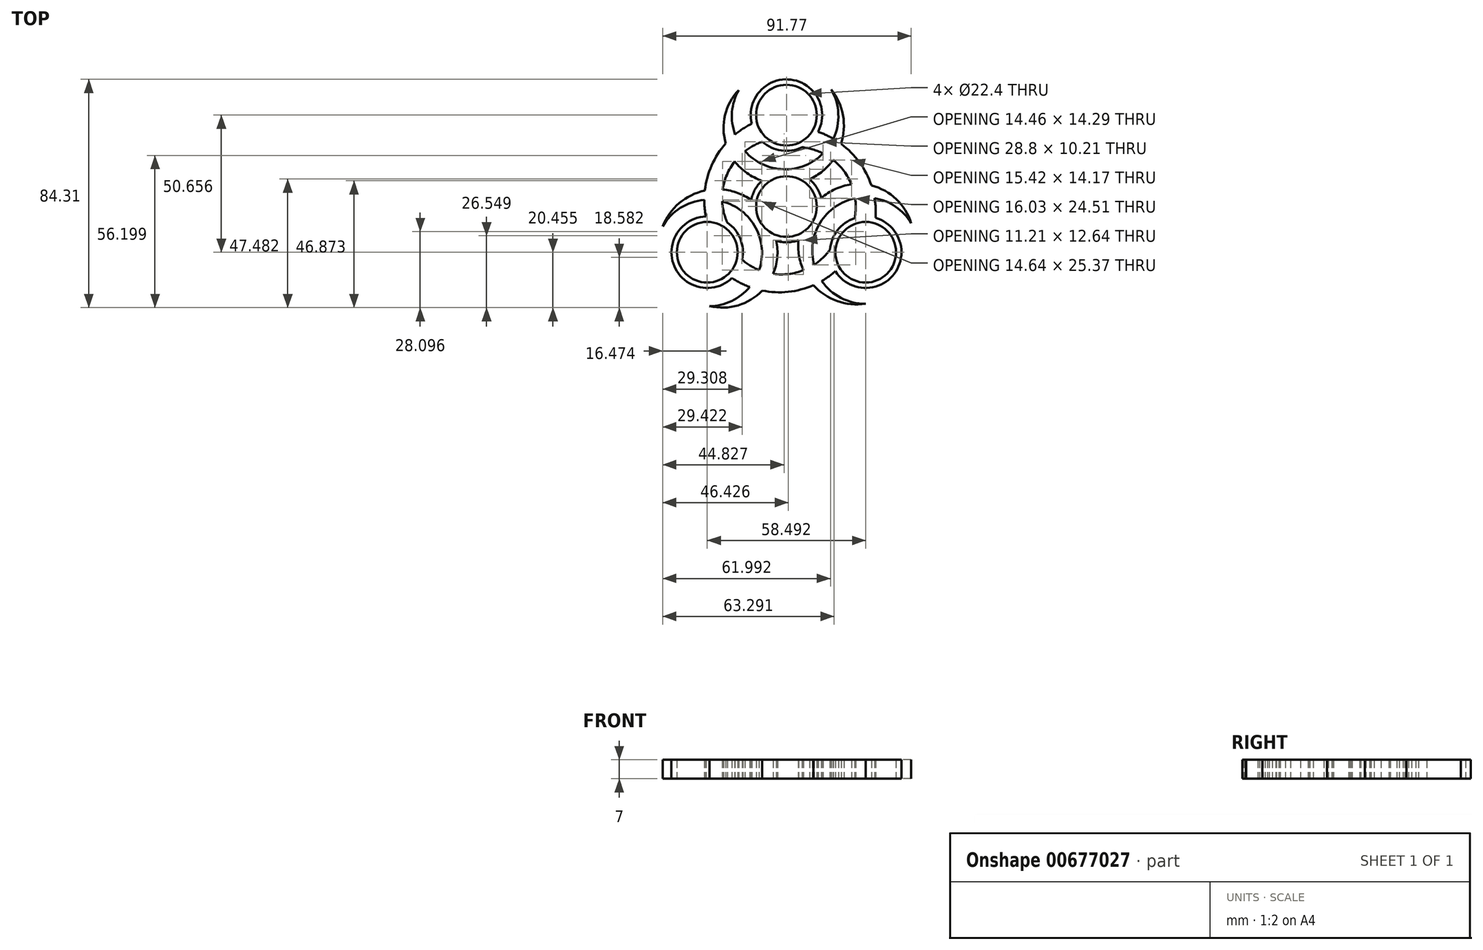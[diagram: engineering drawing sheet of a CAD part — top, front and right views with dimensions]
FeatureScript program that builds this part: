
annotation { "Feature Type Name" : "Feature", "Feature Type Description" : "" }
export const myFeature = defineFeature(function(context is Context, id is Id, definition is map)
    precondition{}
    {
        {
            var Q0;
            Q0=qCreatedBy(makeId("Top.planeOp"),FACE);
            var sketch = newSketch(context, id + "F0", { "sketchPlane" : qUnion([Q0])});
            skCircle(sketch, "E0", {"center": v(0, 0) * mm, "radius": 11.2 * mm});
            skCircle(sketch, "E1", {"center": v(0, 0) * mm, "radius": 13.2 * mm});
            skCircle(sketch, "E2", {"center": v(0, 33.77) * mm, "radius": 11.2 * mm});
            skCircle(sketch, "E3", {"center": v(0, 33.77) * mm, "radius": 13.2 * mm});
            skCircle(sketch, "E4.1.0", {"center": v(-29.25, -16.89) * mm, "radius": 13.2 * mm});
            skCircle(sketch, "E4.1.1", {"center": v(-29.25, -16.89) * mm, "radius": 11.2 * mm});
            skCircle(sketch, "E4.2.0", {"center": v(29.25, -16.89) * mm, "radius": 13.2 * mm});
            skCircle(sketch, "E4.2.1", {"center": v(29.25, -16.89) * mm, "radius": 11.2 * mm});
            skArc(sketch, "E5", {"start": v(-17.68, 42.97) * mm, "mid": v(-0.33, 13.75) * mm, "end": v(16.53, 43.26) * mm});
            skArc(sketch, "E6", {"start": v(8.56, 10.05) * mm, "mid": v(20.61, 24.72) * mm, "end": v(16.53, 43.26) * mm});
            skArc(sketch, "E7", {"start": v(-17.68, 42.97) * mm, "mid": v(-22.58, 23.9) * mm, "end": v(-9.07, 9.6) * mm});
            skArc(sketch, "E8.1.0", {"start": v(-12.98, 2.39) * mm, "mid": v(-31.71, 5.5) * mm, "end": v(-45.72, -7.32) * mm});
            skArc(sketch, "E8.1.1", {"start": v(-28.37, -36.8) * mm, "mid": v(-11.74, -7.16) * mm, "end": v(-45.72, -7.32) * mm});
            skArc(sketch, "E8.1.2", {"start": v(-28.37, -36.8) * mm, "mid": v(-9.4, -31.51) * mm, "end": v(-3.78, -12.65) * mm});
            skArc(sketch, "E8.2.0", {"start": v(4.42, -12.44) * mm, "mid": v(11.1, -30.21) * mm, "end": v(29.2, -35.94) * mm});
            skArc(sketch, "E8.2.1", {"start": v(46.05, -6.18) * mm, "mid": v(12.07, -6.59) * mm, "end": v(29.2, -35.94) * mm});
            skArc(sketch, "E8.2.2", {"start": v(46.05, -6.18) * mm, "mid": v(32, 7.6) * mm, "end": v(12.84, 3.05) * mm});
            skArc(sketch, "E9", {"start": v(-12.82, 30.61) * mm, "mid": v(-27.09, 16.32) * mm, "end": v(-29.73, -3.7) * mm});
            skArc(sketch, "E10", {"start": v(-8.83, 23.96) * mm, "mid": v(-21.94, 11.86) * mm, "end": v(-21.81, -5.98) * mm});
            skArc(sketch, "E11.1.0", {"start": v(-16.34, -19.63) * mm, "mid": v(0.7, -24.94) * mm, "end": v(16.08, -15.9) * mm});
            skArc(sketch, "E11.1.1", {"start": v(-20.1, -26.4) * mm, "mid": v(-0.6, -31.62) * mm, "end": v(18.07, -23.9) * mm});
            skArc(sketch, "E11.2.0", {"start": v(25.17, -4.33) * mm, "mid": v(21.25, 13.07) * mm, "end": v(5.73, 21.88) * mm});
            skArc(sketch, "E11.2.1", {"start": v(32.92, -4.2) * mm, "mid": v(27.68, 15.3) * mm, "end": v(11.67, 27.6) * mm});
            skSolve(sketch);
        }
        {
            var Q0;
            {var subQ5=sQuery(id+"F0.wireOp",EDGE,"E6");var subQ6=sQuery(id+"F0.wireOp",EDGE,"E1");var subQ7=makeQuery(id+"F0.imprint","INTERSECT",VERTEX,{"derivedFrom":[subQ6,subQ5]});Q0=makeQuery(id+"F0.imprint","IMPRINT",FACE,{"disambiguationData":[TD([[makeQuery(id+"F0.imprint","IMPRINT",EDGE,{"disambiguationData":[TD([[subQ7,-1.0]])],"derivedFrom":subQ6}),-1.0]])]});}
            var Q1;
            {var subQ1=sQuery(id+"F0.wireOp",EDGE,"E1");var subQ9=sQuery(id+"F0.wireOp",EDGE,"E8.2.0");var subQ10=makeQuery(id+"F0.imprint","INTERSECT",VERTEX,{"derivedFrom":[subQ1,subQ9]});Q1=makeQuery(id+"F0.imprint","IMPRINT",FACE,{"disambiguationData":[TD([[makeQuery(id+"F0.imprint","IMPRINT",EDGE,{"disambiguationData":[TD([[subQ10,-1.0]])],"derivedFrom":subQ1}),-1.0]])]});}
            var Q2;
            {var subQ1=sQuery(id+"F0.wireOp",EDGE,"E1");var subQ9=sQuery(id+"F0.wireOp",EDGE,"E8.1.0");var subQ10=makeQuery(id+"F0.imprint","INTERSECT",VERTEX,{"derivedFrom":[subQ1,subQ9]});Q2=makeQuery(id+"F0.imprint","IMPRINT",FACE,{"disambiguationData":[TD([[makeQuery(id+"F0.imprint","IMPRINT",EDGE,{"disambiguationData":[TD([[subQ10,-1.0]])],"derivedFrom":subQ1}),-1.0]])]});}
            var Q3;
            Q3=makeQuery(id+"F0.imprint","IMPRINT",FACE,{"disambiguationData":[TD([[makeQuery(id+"F0.imprint","IMPRINT",EDGE,{"derivedFrom":sQuery(id+"F0.wireOp",EDGE,"E0")}),-1.0]])]});
            var Q4;
            Q4=makeQuery(id+"F0.imprint","IMPRINT",FACE,{"disambiguationData":[TD([[makeQuery(id+"F0.imprint","IMPRINT",EDGE,{"derivedFrom":sQuery(id+"F0.wireOp",EDGE,"E4.2.1")}),-1.0]])]});
            var Q5;
            Q5=makeQuery(id+"F0.imprint","IMPRINT",FACE,{"disambiguationData":[TD([[makeQuery(id+"F0.imprint","IMPRINT",EDGE,{"derivedFrom":sQuery(id+"F0.wireOp",EDGE,"E4.1.1")}),-1.0]])]});
            var Q6;
            Q6=makeQuery(id+"F0.imprint","IMPRINT",FACE,{"disambiguationData":[TD([[makeQuery(id+"F0.imprint","IMPRINT",EDGE,{"derivedFrom":sQuery(id+"F0.wireOp",EDGE,"E2")}),-1.0]])]});
            var Q7;
            {var subQ0=sQuery(id+"F0.wireOp",EDGE,"E11.2.1");var subQ1=sQuery(id+"F0.wireOp",EDGE,"E6");var subQ2=makeQuery(id+"F0.imprint","INTERSECT",VERTEX,{"derivedFrom":[subQ1,subQ0]});Q7=makeQuery(id+"F0.imprint","IMPRINT",FACE,{"disambiguationData":[TD([[makeQuery(id+"F0.imprint","IMPRINT",EDGE,{"disambiguationData":[TD([[subQ2,1.0]])],"derivedFrom":subQ1}),-1.0]])]});}
            var Q8;
            {var subQ0=sQuery(id+"F0.wireOp",EDGE,"E11.2.0");var subQ1=sQuery(id+"F0.wireOp",EDGE,"E3");var subQ2=makeQuery(id+"F0.imprint","INTERSECT",VERTEX,{"derivedFrom":[subQ1,subQ0]});Q8=makeQuery(id+"F0.imprint","IMPRINT",FACE,{"disambiguationData":[TD([[makeQuery(id+"F0.imprint","IMPRINT",EDGE,{"disambiguationData":[TD([[subQ2,-1.0]])],"derivedFrom":subQ1}),-1.0]])]});}
            var Q9;
            {var subQ0=sQuery(id+"F0.wireOp",EDGE,"E11.2.1");var subQ1=sQuery(id+"F0.wireOp",EDGE,"E5");var subQ2=makeQuery(id+"F0.imprint","INTERSECT",VERTEX,{"derivedFrom":[subQ1,subQ0]});Q9=makeQuery(id+"F0.imprint","IMPRINT",FACE,{"disambiguationData":[TD([[makeQuery(id+"F0.imprint","IMPRINT",EDGE,{"disambiguationData":[TD([[subQ2,1.0]])],"derivedFrom":subQ1}),-1.0]])]});}
            var Q10;
            {var subQ0=sQuery(id+"F0.wireOp",EDGE,"E11.2.1");var subQ1=sQuery(id+"F0.wireOp",EDGE,"E8.2.1");var subQ2=makeQuery(id+"F0.imprint","INTERSECT",VERTEX,{"derivedFrom":[subQ1,subQ0]});Q10=makeQuery(id+"F0.imprint","IMPRINT",FACE,{"disambiguationData":[TD([[makeQuery(id+"F0.imprint","IMPRINT",EDGE,{"disambiguationData":[TD([[subQ2,-1.0]])],"derivedFrom":subQ1}),-1.0]])]});}
            var Q11;
            {var subQ0=sQuery(id+"F0.wireOp",EDGE,"E11.2.0");var subQ1=sQuery(id+"F0.wireOp",EDGE,"E4.2.0");var subQ2=makeQuery(id+"F0.imprint","INTERSECT",VERTEX,{"derivedFrom":[subQ1,subQ0]});Q11=makeQuery(id+"F0.imprint","IMPRINT",FACE,{"disambiguationData":[TD([[makeQuery(id+"F0.imprint","IMPRINT",EDGE,{"disambiguationData":[TD([[subQ2,1.0]])],"derivedFrom":subQ1}),-1.0]])]});}
            var Q12;
            {var subQ0=sQuery(id+"F0.wireOp",EDGE,"E8.2.2");var subQ1=sQuery(id+"F0.wireOp",EDGE,"E8.2.1");var subQ2=makeQuery(id+"F0.imprint","INTERSECT",VERTEX,{"derivedFrom":[subQ1,subQ0]});Q12=makeQuery(id+"F0.imprint","IMPRINT",FACE,{"disambiguationData":[TD([[makeQuery(id+"F0.imprint","IMPRINT",EDGE,{"disambiguationData":[TD([[subQ2,-1.0]])],"derivedFrom":subQ1}),-1.0]])]});}
            var Q13;
            {var subQ0=sQuery(id+"F0.wireOp",EDGE,"E6");var subQ1=sQuery(id+"F0.wireOp",EDGE,"E5");var subQ2=makeQuery(id+"F0.imprint","INTERSECT",VERTEX,{"derivedFrom":[subQ1,subQ0]});Q13=makeQuery(id+"F0.imprint","IMPRINT",FACE,{"disambiguationData":[TD([[makeQuery(id+"F0.imprint","IMPRINT",EDGE,{"disambiguationData":[TD([[subQ2,1.0]])],"derivedFrom":subQ1}),-1.0]])]});}
            var Q14;
            {var subQ0=sQuery(id+"F0.wireOp",EDGE,"E9");var subQ1=sQuery(id+"F0.wireOp",EDGE,"E5");var subQ2=makeQuery(id+"F0.imprint","INTERSECT",VERTEX,{"derivedFrom":[subQ1,subQ0]});Q14=makeQuery(id+"F0.imprint","IMPRINT",FACE,{"disambiguationData":[TD([[makeQuery(id+"F0.imprint","IMPRINT",EDGE,{"disambiguationData":[TD([[subQ2,-1.0]])],"derivedFrom":subQ1}),-1.0]])]});}
            var Q15;
            {var subQ0=sQuery(id+"F0.wireOp",EDGE,"E9");var subQ1=sQuery(id+"F0.wireOp",EDGE,"E3");var subQ2=makeQuery(id+"F0.imprint","INTERSECT",VERTEX,{"derivedFrom":[subQ1,subQ0]});Q15=makeQuery(id+"F0.imprint","IMPRINT",FACE,{"disambiguationData":[TD([[makeQuery(id+"F0.imprint","IMPRINT",EDGE,{"disambiguationData":[TD([[subQ2,-1.0]])],"derivedFrom":subQ1}),-1.0]])]});}
            var Q16;
            {var subQ0=sQuery(id+"F0.wireOp",EDGE,"E7");var subQ1=sQuery(id+"F0.wireOp",EDGE,"E5");var subQ2=makeQuery(id+"F0.imprint","INTERSECT",VERTEX,{"derivedFrom":[subQ1,subQ0]});Q16=makeQuery(id+"F0.imprint","IMPRINT",FACE,{"disambiguationData":[TD([[makeQuery(id+"F0.imprint","IMPRINT",EDGE,{"disambiguationData":[TD([[subQ2,-1.0]])],"derivedFrom":subQ1}),-1.0]])]});}
            var Q17;
            {var subQ0=sQuery(id+"F0.wireOp",EDGE,"E9");var subQ1=sQuery(id+"F0.wireOp",EDGE,"E7");var subQ2=makeQuery(id+"F0.imprint","INTERSECT",VERTEX,{"derivedFrom":[subQ1,subQ0]});Q17=makeQuery(id+"F0.imprint","IMPRINT",FACE,{"disambiguationData":[TD([[makeQuery(id+"F0.imprint","IMPRINT",EDGE,{"disambiguationData":[TD([[subQ2,-1.0]])],"derivedFrom":subQ1}),-1.0]])]});}
            var Q18;
            {var subQ0=sQuery(id+"F0.wireOp",EDGE,"E9");var subQ1=sQuery(id+"F0.wireOp",EDGE,"E8.1.0");var subQ2=makeQuery(id+"F0.imprint","INTERSECT",VERTEX,{"derivedFrom":[subQ1,subQ0]});Q18=makeQuery(id+"F0.imprint","IMPRINT",FACE,{"disambiguationData":[TD([[makeQuery(id+"F0.imprint","IMPRINT",EDGE,{"disambiguationData":[TD([[subQ2,1.0]])],"derivedFrom":subQ1}),1.0]])]});}
            var Q19;
            {var subQ0=sQuery(id+"F0.wireOp",EDGE,"E8.1.1");var subQ1=sQuery(id+"F0.wireOp",EDGE,"E8.1.0");var subQ2=makeQuery(id+"F0.imprint","INTERSECT",VERTEX,{"derivedFrom":[subQ1,subQ0]});Q19=makeQuery(id+"F0.imprint","IMPRINT",FACE,{"disambiguationData":[TD([[makeQuery(id+"F0.imprint","IMPRINT",EDGE,{"disambiguationData":[TD([[subQ2,1.0]])],"derivedFrom":subQ1}),1.0]])]});}
            var Q20;
            {var subQ0=sQuery(id+"F0.wireOp",EDGE,"E9");var subQ1=sQuery(id+"F0.wireOp",EDGE,"E4.1.0");var subQ2=makeQuery(id+"F0.imprint","INTERSECT",VERTEX,{"derivedFrom":[subQ1,subQ0]});Q20=makeQuery(id+"F0.imprint","IMPRINT",FACE,{"disambiguationData":[TD([[makeQuery(id+"F0.imprint","IMPRINT",EDGE,{"disambiguationData":[TD([[subQ2,1.0]])],"derivedFrom":subQ1}),-1.0]])]});}
            var Q21;
            {var subQ0=sQuery(id+"F0.wireOp",EDGE,"E11.1.0");var subQ1=sQuery(id+"F0.wireOp",EDGE,"E4.2.0");var subQ2=makeQuery(id+"F0.imprint","INTERSECT",VERTEX,{"derivedFrom":[subQ1,subQ0]});Q21=makeQuery(id+"F0.imprint","IMPRINT",FACE,{"disambiguationData":[TD([[makeQuery(id+"F0.imprint","IMPRINT",EDGE,{"disambiguationData":[TD([[subQ2,-1.0]])],"derivedFrom":subQ1}),-1.0]])]});}
            var Q22;
            {var subQ0=sQuery(id+"F0.wireOp",EDGE,"E11.1.1");var subQ1=sQuery(id+"F0.wireOp",EDGE,"E8.2.0");var subQ2=makeQuery(id+"F0.imprint","INTERSECT",VERTEX,{"derivedFrom":[subQ1,subQ0]});Q22=makeQuery(id+"F0.imprint","IMPRINT",FACE,{"disambiguationData":[TD([[makeQuery(id+"F0.imprint","IMPRINT",EDGE,{"disambiguationData":[TD([[subQ2,1.0]])],"derivedFrom":subQ1}),1.0]])]});}
            var Q23;
            {var subQ0=sQuery(id+"F0.wireOp",EDGE,"E8.2.1");var subQ1=sQuery(id+"F0.wireOp",EDGE,"E8.2.0");var subQ2=makeQuery(id+"F0.imprint","INTERSECT",VERTEX,{"derivedFrom":[subQ1,subQ0]});Q23=makeQuery(id+"F0.imprint","IMPRINT",FACE,{"disambiguationData":[TD([[makeQuery(id+"F0.imprint","IMPRINT",EDGE,{"disambiguationData":[TD([[subQ2,1.0]])],"derivedFrom":subQ1}),1.0]])]});}
            var Q24;
            {var subQ0=sQuery(id+"F0.wireOp",EDGE,"E11.1.1");var subQ1=sQuery(id+"F0.wireOp",EDGE,"E8.1.2");var subQ2=makeQuery(id+"F0.imprint","INTERSECT",VERTEX,{"derivedFrom":[subQ1,subQ0]});Q24=makeQuery(id+"F0.imprint","IMPRINT",FACE,{"disambiguationData":[TD([[makeQuery(id+"F0.imprint","IMPRINT",EDGE,{"disambiguationData":[TD([[subQ2,-1.0]])],"derivedFrom":subQ1}),-1.0]])]});}
            var Q25;
            {var subQ0=sQuery(id+"F0.wireOp",EDGE,"E11.1.1");var subQ1=sQuery(id+"F0.wireOp",EDGE,"E8.1.1");var subQ2=makeQuery(id+"F0.imprint","INTERSECT",VERTEX,{"derivedFrom":[subQ1,subQ0]});Q25=makeQuery(id+"F0.imprint","IMPRINT",FACE,{"disambiguationData":[TD([[makeQuery(id+"F0.imprint","IMPRINT",EDGE,{"disambiguationData":[TD([[subQ2,-1.0]])],"derivedFrom":subQ1}),-1.0]])]});}
            var Q26;
            {var subQ0=sQuery(id+"F0.wireOp",EDGE,"E11.1.0");var subQ1=sQuery(id+"F0.wireOp",EDGE,"E4.1.0");var subQ2=makeQuery(id+"F0.imprint","INTERSECT",VERTEX,{"derivedFrom":[subQ1,subQ0]});Q26=makeQuery(id+"F0.imprint","IMPRINT",FACE,{"disambiguationData":[TD([[makeQuery(id+"F0.imprint","IMPRINT",EDGE,{"disambiguationData":[TD([[subQ2,1.0]])],"derivedFrom":subQ1}),-1.0]])]});}
            var Q27;
            {var subQ0=sQuery(id+"F0.wireOp",EDGE,"E8.1.2");var subQ1=sQuery(id+"F0.wireOp",EDGE,"E8.1.1");var subQ2=makeQuery(id+"F0.imprint","INTERSECT",VERTEX,{"derivedFrom":[subQ1,subQ0]});Q27=makeQuery(id+"F0.imprint","IMPRINT",FACE,{"disambiguationData":[TD([[makeQuery(id+"F0.imprint","IMPRINT",EDGE,{"disambiguationData":[TD([[subQ2,-1.0]])],"derivedFrom":subQ1}),-1.0]])]});}
            extrude(context, id + "F1", {"entities" : qUnion([Q0, Q1, Q2, Q3, Q4, Q5, Q6, Q7, Q8, Q9, Q10, Q11, Q12, Q13, Q14, Q15, Q16, Q17, Q18, Q19, Q20, Q21, Q22, Q23, Q24, Q25, Q26, Q27]), "depth" : 7 * mm, "offsetDistance" : 25 * mm});
        }
    });
